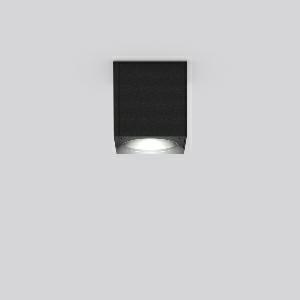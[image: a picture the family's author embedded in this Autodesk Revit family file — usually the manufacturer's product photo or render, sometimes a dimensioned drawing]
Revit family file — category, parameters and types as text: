
# Revit family: hb_111_931187_0031_80df
name_source: partatom
category: Lighting Fixtures
units: mm (PartAtom-declared; Revit-internal decimal feet)

## family parameters
Cut with Voids When Loaded = No
Host = Face
Light Source = No
Part Type = Normal
Room Calculation Point = No
Round Connector Dimension = Use Diameter
Shared = No

## types (1)
- HB 111 (1 x LED Modul 830, 590 lm, 3000)
    Apparent Load = 9 VA
    CIE Flux Codes = 64 91 96 87 100
    Color Rendering = 80
    Color Temperature = 3000
    Default Elevation = 1800 mm
    Description = Series: HB 111
Square surface-mounted downlight for outdoor use. Housing: die-cast aluminium, powder-coated. Clear glass cover. Driver integrated. 
Colour: anthracite metallic (DB703)
Length: 90 mm
Width: 90 mm
Height: 94 mm
Lamp: LED
System power: 9 W
Rated luminous flux: 590 lm
Luminous efficiency: 66 lm/W
Control gear: Regulated power supply
Protection class: I
Type of protection: IP 54
    Height = 94 mm  [stored 0.308399 ft]
    Lamp = 1 x LED Modul 830
    Lamp Light Flux = 590 lm
    Lamp count = 1
    Length = 90 mm
    Lifetime = 50000 h
    Luminous efficacy = 66 lm/W
    Manufacturer = RZB
    ModVariant = No
    Model = 931187.0031
    Mounting Place = Ceiling
    Mounting Type = Surface mounted
    Number of Poles = 1
    OnlyDefault = Yes
    Power Factor = 1
    Product Name = HB 111
    Product group = Surface mounted ceiling luminaires
    ProductGroupID = 303
    Protection Class = Protection class I
    Protection Degree = IP 54
    RLX_Detail_Level = 1
    RLX_Emergency_Light_Flux = 0 lm
    RLX_Emergency_Type = 0
    RLX_Emergency_Type_DB = No
    RlxData = <blob elided: 23149 chars, md5=cb30f108>
    Socket = socket
    Standby Power = 0 W
    System Light Flux = 590 lm
    System Power = 9 W
    Type Comments = Product without accessories
    Type Image = 931187.0031.jpg
    URL = http://relux.com
    VarID = ---
    Voltage = 230 V
    Voltage Range = 220-240 V
    Weight = 0.00 kg
    Width = 90 mm

note: [stored X ft] marks values corroborated as IEEE doubles in the binary element streams (Revit-internal decimal feet)

## geometry (parser evidence)
native form markers: Blend x4, Sweep x12
no freeform markers — native parametric forms only
